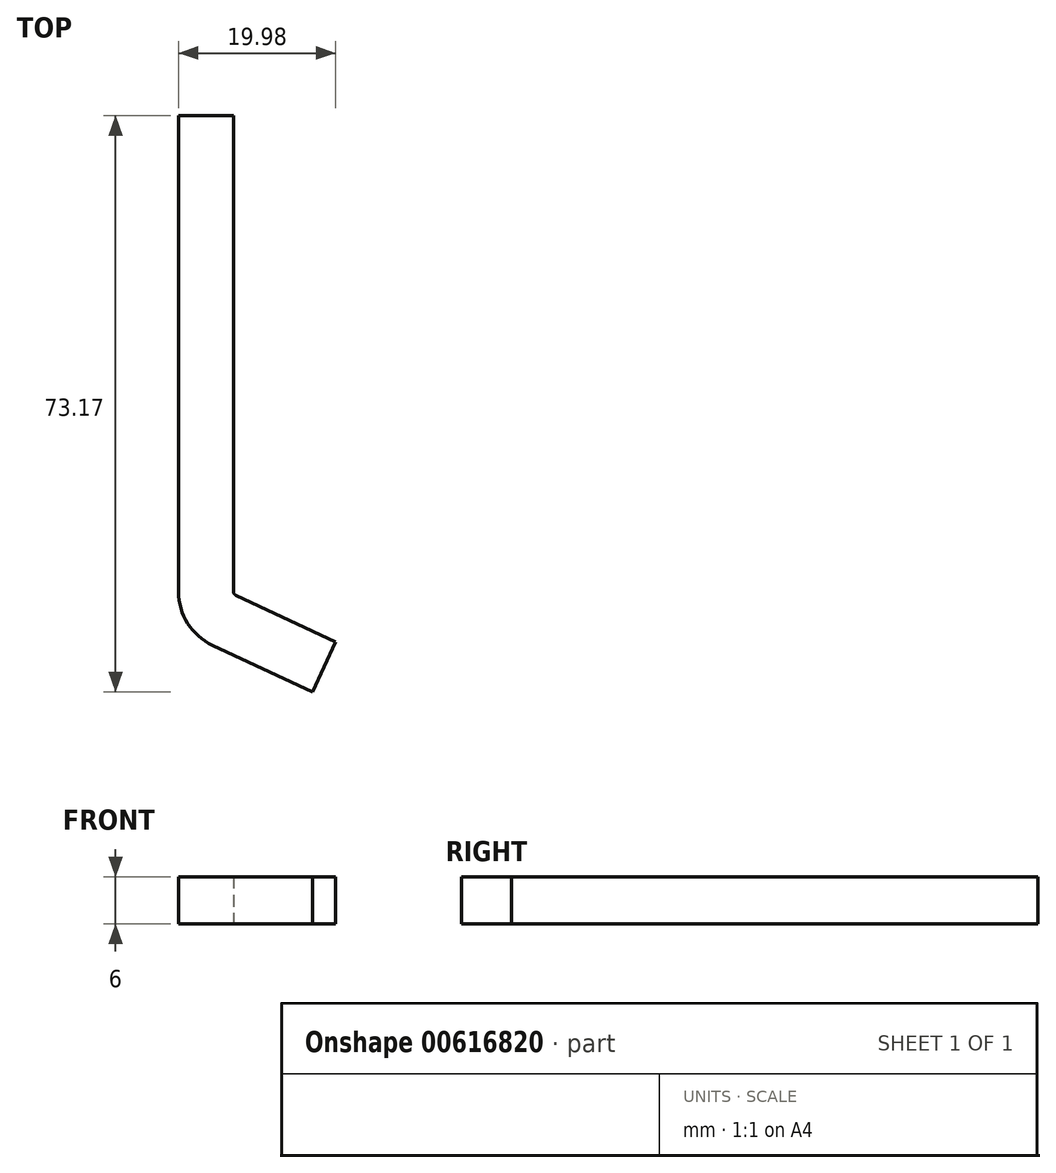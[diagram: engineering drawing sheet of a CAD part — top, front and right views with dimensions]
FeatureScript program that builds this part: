
annotation { "Feature Type Name" : "Feature", "Feature Type Description" : "" }
export const myFeature = defineFeature(function(context is Context, id is Id, definition is map)
    precondition{}
    {
        {
            var Q0;
            Q0=qCreatedBy(makeId("Front.planeOp"),FACE);
            var sketch = newSketch(context, id + "F0", { "sketchPlane" : qUnion([Q0])});
            skLineSegment(sketch, "E0.bottom", {"start": v(3.5, 3) * mm, "end": v(-3.5, 3) * mm});
            skLineSegment(sketch, "E0.top", {"start": v(3.5, -3) * mm, "end": v(-3.5, -3) * mm});
            skLineSegment(sketch, "E0.left", {"start": v(3.5, 3) * mm, "end": v(3.5, -3) * mm});
            skLineSegment(sketch, "E0.right", {"start": v(-3.5, 3) * mm, "end": v(-3.5, -3) * mm});
            skPoint(sketch, "E0.middle", {"position": v(0, 0) * mm});
            skSolve(sketch);
        }
        {
            var Q0;
            Q0=qCreatedBy(makeId("Top.planeOp"),FACE);
            var sketch = newSketch(context, id + "F1", { "sketchPlane" : qUnion([Q0])});
            skLineSegment(sketch, "E1", {"start": v(0, 0) * mm, "end": v(0, -60.46) * mm});
            skLineSegment(sketch, "E2", {"start": v(2.3, -64.08) * mm, "end": v(15, -70) * mm});
            skPoint(sketch, "E3.visualSharp", {"position": v(0, -63) * mm});
            skArc(sketch, "E3.filletArc", {"start": v(0, -60.46) * mm, "mid": v(0.63, -62.6) * mm, "end": v(2.3, -64.08) * mm});
            skSolve(sketch);
        }
        {
            var Q0;
            Q0=makeQuery(id+"F0.imprint","IMPRINT",FACE,{"disambiguationData":[TD([[makeQuery(id+"F0.imprint","IMPRINT",EDGE,{"derivedFrom":sQuery(id+"F0.wireOp",EDGE,"E0.bottom")}),1.0]])]});
            var Q1;
            Q1=sQuery(id+"F1.wireOp",EDGE,"E1");
            var Q2;
            Q2=sQuery(id+"F1.wireOp",EDGE,"E2");
            var Q3;
            Q3=sQuery(id+"F1.wireOp",EDGE,"E3.filletArc");
            sweep(context, id + "F2", {"profiles" : qUnion([Q0]), "path" : qUnion([Q1, Q2, Q3])});
        }
    });
